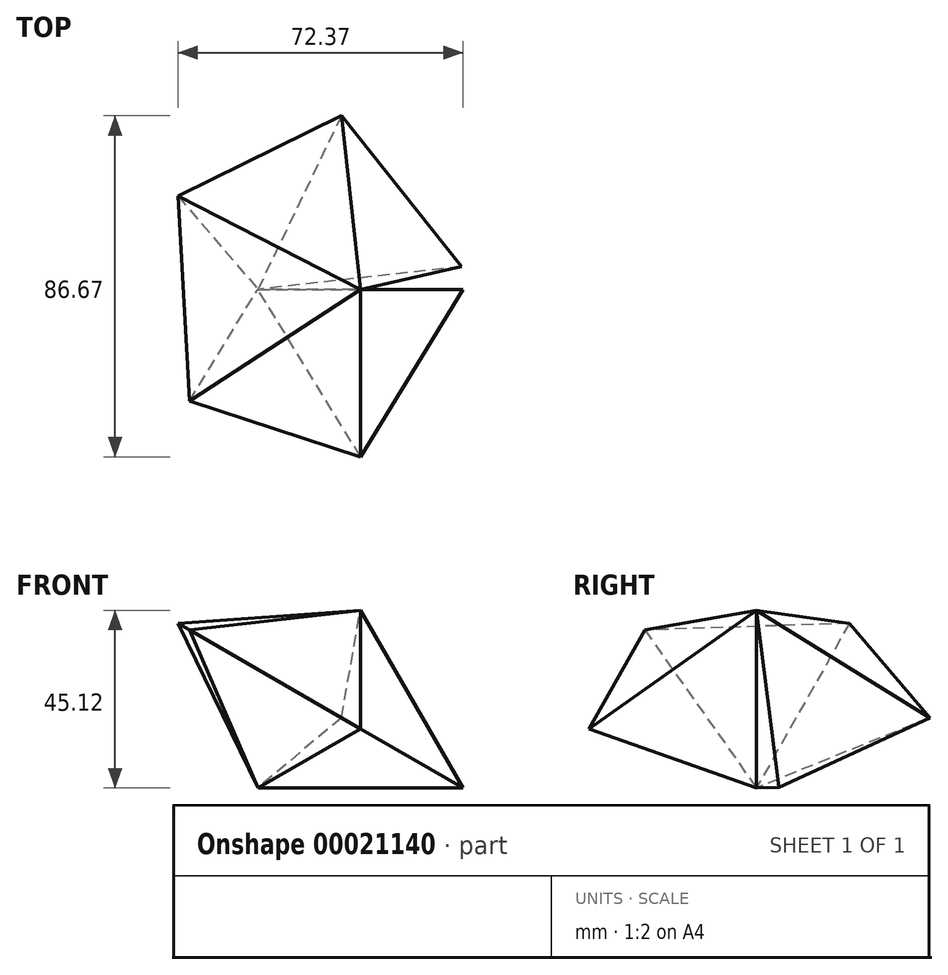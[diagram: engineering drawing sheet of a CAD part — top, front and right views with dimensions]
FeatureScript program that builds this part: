
annotation { "Feature Type Name" : "Feature", "Feature Type Description" : "" }
export const myFeature = defineFeature(function(context is Context, id is Id, definition is map)
    precondition{}
    {
        {
            var Q0;
            Q0=qCreatedBy(makeId("Front.planeOp"),FACE);
            var sketch = newSketch(context, id + "F0", { "sketchPlane" : qUnion([Q0])});
            skLineSegment(sketch, "E0", {"start": v(-26.05, -20.15) * mm, "end": v(26.05, -20.15) * mm});
            skLineSegment(sketch, "E1", {"start": v(26.05, -20.15) * mm, "end": v(0, 24.97) * mm});
            skLineSegment(sketch, "E2", {"start": v(0, 24.97) * mm, "end": v(-26.05, -20.15) * mm});
            skSolve(sketch);
        }
        {
            var Q0;
            Q0=makeQuery(id+"F0.imprint","IMPRINT",FACE,{"disambiguationData":[TD([[makeQuery(id+"F0.imprint","IMPRINT",EDGE,{"derivedFrom":sQuery(id+"F0.wireOp",EDGE,"E0")}),1.0]])]});
            extrude(context, id + "F1", {"entities" : qUnion([Q0]), "depth" : 50.8 * mm, "hasDraft" : true, "draftAngle" : 19.47 * degree, "draftPullDirection" : true});
        }
        {
            var Q0;
            Q0=makeQuery(id+"F1.opExtrude","SWEPT_BODY",BODY,{"disambiguationData":[OSD([sQuery(id+"F0.wireOp",EDGE,"E0"),sQuery(id+"F0.wireOp",EDGE,"E1"),sQuery(id+"F0.wireOp",EDGE,"E2")])]});
            var Q1;
            Q1=sQuery(id+"F0.wireOp",EDGE,"E2");
            circularPattern(context, id + "F2", {"entities" : qUnion([Q0]), "axis" : qUnion([Q1]), "angle" : 70.53 * degree, "instanceCount" : 5});
        }
    });
